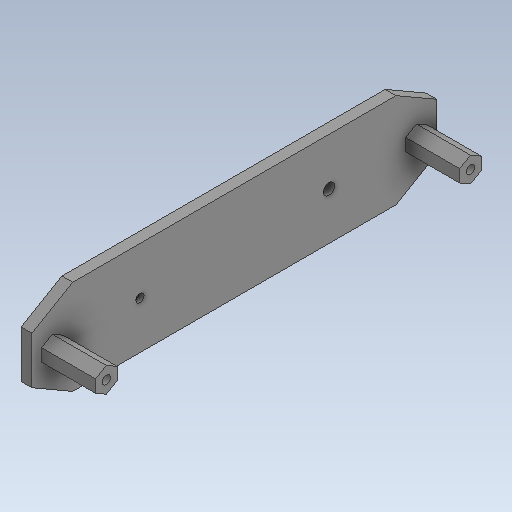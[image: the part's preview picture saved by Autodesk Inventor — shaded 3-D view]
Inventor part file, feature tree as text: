
AUTODESK INVENTOR PART (.ipt)
format: ipt  version: 2020 (Build 240168000, 168)  size: 228,864 bytes
history: native  units: in
note: dims shown in document units (in); Inventor stores cm internally (conversion verified against a paired STEP export)
features: extrude x7, sketch x7, plane x1
ambient origin geometry x8: Origin, YZ Plane, XZ Plane, XY Plane, X Axis, Y Axis, Z Axis, Center Point
bodies: Solid1 (feature_tree)
feature tree (15):
  extrude  "Extrusion1"  Depth=5.9055in
  extrude  "Extrusion3"  TaperAngle=0.0deg  [1 undecoded]
  extrude  "Extrusion4"  Depth=0.7874in
  plane  "Work Plane1"
  extrude  "Extrusion5"  Depth=0.122in
  extrude  "Extrusion6"  Depth=0.2402in
  extrude  "Extrusion7"  [1 undecoded]
  extrude  "Extrusion8"  Depth=0.0866in TaperAngle=0.0deg
  sketch  "Sketch1"  dims[d0=1.378in d1=5.9055in]
  sketch  "Sketch2"  dims[d2=0.1575in d3=0.0in]
  sketch  "Sketch3"  dims[d8=0.315in d9=0.7874in]
  sketch  "Sketch4"  dims[d10=0.0in d12=0.122in]
  sketch  "Sketch5"  dims[d13=0.0in d14=0.0in d15=0.2402in]
  sketch  "Sketch8"  dims[d16=0.0866in d17=-0.2233in]
  sketch  "Sketch9"  dims[d18=-0.3937in d19=0.0866in d20=0.0in d26=1.5748in d27=0.1654in d28=0.122in d29=1.5748in d30=0.0in d31=0.0in d32=0.2402in d33=0.0866in d34=-0.2233in]
note: 2 required parameter values undecoded (feature->parameter linkage not recoverable at this tier; creation-order binding heuristic only, values carry confidence <= 0.55)
